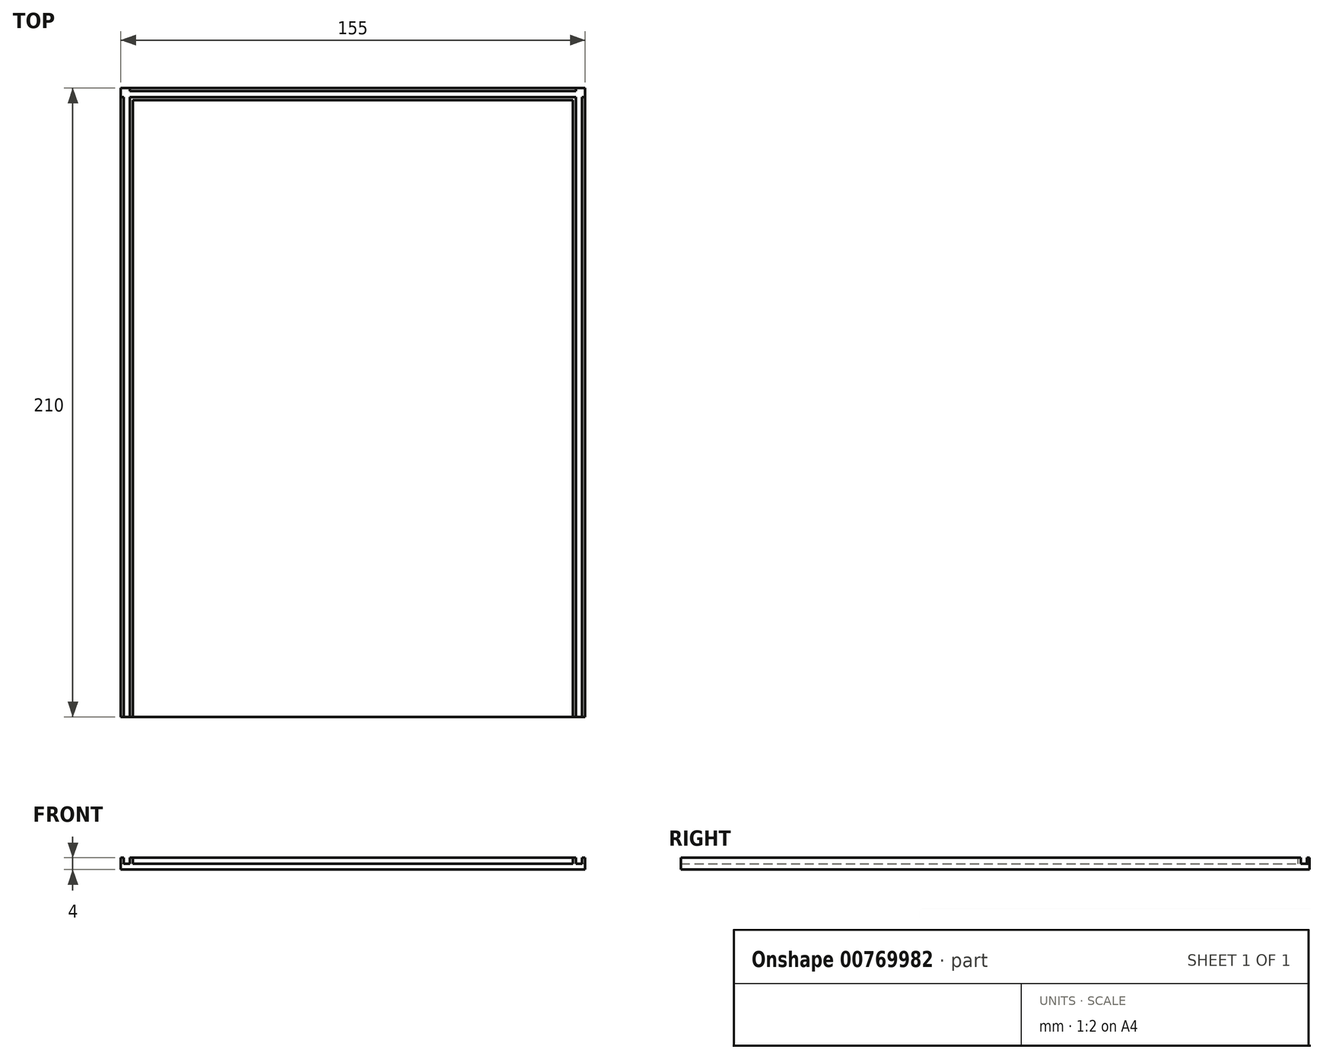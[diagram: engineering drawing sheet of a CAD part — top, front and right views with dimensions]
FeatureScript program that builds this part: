
annotation { "Feature Type Name" : "Feature", "Feature Type Description" : "" }
export const myFeature = defineFeature(function(context is Context, id is Id, definition is map)
    precondition{}
    {
        {
            var Q0;
            Q0=qCreatedBy(makeId("Top.planeOp"),FACE);
            var sketch = newSketch(context, id + "F0", { "sketchPlane" : qUnion([Q0])});
            skPoint(sketch, "E0.middle", {"position": v(0, 0) * mm});
            skLineSegment(sketch, "E1.bottom", {"start": v(77.5, 105) * mm, "end": v(-77.5, 105) * mm});
            skLineSegment(sketch, "E1.top", {"start": v(77.5, -105) * mm, "end": v(-77.5, -105) * mm});
            skLineSegment(sketch, "E1.left", {"start": v(77.5, 105) * mm, "end": v(77.5, -105) * mm});
            skLineSegment(sketch, "E1.right", {"start": v(-77.5, 105) * mm, "end": v(-77.5, -105) * mm});
            skLineSegment(sketch, "E2", {"start": v(-76.5, 105) * mm, "end": v(-76.5, 104) * mm});
            skLineSegment(sketch, "E3", {"start": v(-74.5, 105) * mm, "end": v(-74.5, 104) * mm});
            skLineSegment(sketch, "E4", {"start": v(-73.5, 105) * mm, "end": v(-73.5, 104) * mm});
            skLineSegment(sketch, "E5.MirrorCS", {"start": v(76.5, 105) * mm, "end": v(76.5, 104) * mm});
            skLineSegment(sketch, "E6.MirrorCS", {"start": v(73.5, 105) * mm, "end": v(73.5, 104) * mm});
            skLineSegment(sketch, "E7.MirrorCS", {"start": v(74.5, 105) * mm, "end": v(74.5, 104) * mm});
            skLineSegment(sketch, "E8", {"start": v(-77.5, 104) * mm, "end": v(77.5, 104) * mm});
            skLineSegment(sketch, "E9", {"start": v(-77.5, 102) * mm, "end": v(77.5, 102) * mm});
            skLineSegment(sketch, "E10", {"start": v(-77.5, 101) * mm, "end": v(77.5, 101) * mm});
            skLineSegment(sketch, "E11.trimOffspring", {"start": v(-76.5, 102) * mm, "end": v(-76.5, -105) * mm});
            skLineSegment(sketch, "E12.trimOffspring", {"start": v(-74.5, 102) * mm, "end": v(-74.5, -105) * mm});
            skLineSegment(sketch, "E13.trimOffspring", {"start": v(-73.5, 102) * mm, "end": v(-73.5, -105) * mm});
            skLineSegment(sketch, "E14.trimOffspring", {"start": v(73.5, 102) * mm, "end": v(73.5, -105) * mm});
            skLineSegment(sketch, "E15.trimOffspring", {"start": v(74.5, 102) * mm, "end": v(74.5, -105) * mm});
            skLineSegment(sketch, "E16.trimOffspring", {"start": v(76.5, 102) * mm, "end": v(76.5, -105) * mm});
            skSolve(sketch);
        }
        {
            var Q0;
            {var subQ0=sQuery(id+"F0.wireOp",EDGE,"E13.trimOffspring");var subQ1=sQuery(id+"F0.wireOp",EDGE,"E1.top");var subQ2=makeQuery(id+"F0.imprint","INTERSECT",VERTEX,{"derivedFrom":[subQ1,subQ0]});Q0=makeQuery(id+"F0.imprint","IMPRINT",FACE,{"disambiguationData":[TD([[makeQuery(id+"F0.imprint","IMPRINT",EDGE,{"disambiguationData":[TD([[subQ2,1.0]])],"derivedFrom":subQ1}),-1.0]])]});}
            var Q1;
            {var subQ4=sQuery(id+"F0.wireOp",EDGE,"E8");var subQ6=sQuery(id+"F0.wireOp",EDGE,"E1.left");var subQ7=makeQuery(id+"F0.imprint","INTERSECT",VERTEX,{"derivedFrom":[subQ6,subQ4]});Q1=makeQuery(id+"F0.imprint","IMPRINT",FACE,{"disambiguationData":[TD([[makeQuery(id+"F0.imprint","IMPRINT",EDGE,{"disambiguationData":[TD([[subQ7,-1.0]])],"derivedFrom":subQ6}),-1.0]])]});}
            var Q2;
            {var subQ0=sQuery(id+"F0.wireOp",EDGE,"E15.trimOffspring");var subQ1=sQuery(id+"F0.wireOp",EDGE,"E1.top");var subQ2=makeQuery(id+"F0.imprint","INTERSECT",VERTEX,{"derivedFrom":[subQ1,subQ0]});Q2=makeQuery(id+"F0.imprint","IMPRINT",FACE,{"disambiguationData":[TD([[makeQuery(id+"F0.imprint","IMPRINT",EDGE,{"disambiguationData":[TD([[subQ2,1.0]])],"derivedFrom":subQ1}),-1.0]])]});}
            var Q3;
            {var subQ0=sQuery(id+"F0.wireOp",EDGE,"E11.trimOffspring");var subQ1=sQuery(id+"F0.wireOp",EDGE,"E1.top");var subQ2=makeQuery(id+"F0.imprint","INTERSECT",VERTEX,{"derivedFrom":[subQ1,subQ0]});Q3=makeQuery(id+"F0.imprint","IMPRINT",FACE,{"disambiguationData":[TD([[makeQuery(id+"F0.imprint","IMPRINT",EDGE,{"disambiguationData":[TD([[subQ2,1.0]])],"derivedFrom":subQ1}),-1.0]])]});}
            var Q4;
            {var subQ0=sQuery(id+"F0.wireOp",EDGE,"E13.trimOffspring");var subQ1=sQuery(id+"F0.wireOp",EDGE,"E9");var subQ2=makeQuery(id+"F0.imprint","INTERSECT",VERTEX,{"derivedFrom":[subQ1,subQ0]});Q4=makeQuery(id+"F0.imprint","IMPRINT",FACE,{"disambiguationData":[TD([[makeQuery(id+"F0.imprint","IMPRINT",EDGE,{"disambiguationData":[TD([[subQ2,-1.0]])],"derivedFrom":subQ1}),-1.0]])]});}
            var Q5;
            {var subQ0=sQuery(id+"F0.wireOp",EDGE,"E14.trimOffspring");var subQ1=sQuery(id+"F0.wireOp",EDGE,"E1.top");var subQ2=makeQuery(id+"F0.imprint","INTERSECT",VERTEX,{"derivedFrom":[subQ1,subQ0]});Q5=makeQuery(id+"F0.imprint","IMPRINT",FACE,{"disambiguationData":[TD([[makeQuery(id+"F0.imprint","IMPRINT",EDGE,{"disambiguationData":[TD([[subQ2,1.0]])],"derivedFrom":subQ1}),-1.0]])]});}
            var Q6;
            {var subQ0=sQuery(id+"F0.wireOp",EDGE,"E12.trimOffspring");var subQ1=sQuery(id+"F0.wireOp",EDGE,"E1.top");var subQ2=makeQuery(id+"F0.imprint","INTERSECT",VERTEX,{"derivedFrom":[subQ1,subQ0]});Q6=makeQuery(id+"F0.imprint","IMPRINT",FACE,{"disambiguationData":[TD([[makeQuery(id+"F0.imprint","IMPRINT",EDGE,{"disambiguationData":[TD([[subQ2,1.0]])],"derivedFrom":subQ1}),-1.0]])]});}
            var Q7;
            {var subQ0=sQuery(id+"F0.wireOp",EDGE,"E4");Q7=makeQuery(id+"F0.imprint","IMPRINT",FACE,{"disambiguationData":[TD([[makeQuery(id+"F0.imprint","IMPRINT",EDGE,{"derivedFrom":subQ0}),1.0]])]});}
            var Q8;
            {var subQ0=sQuery(id+"F0.wireOp",EDGE,"E1.right");var subQ1=sQuery(id+"F0.wireOp",EDGE,"E1.top");var subQ2=makeQuery(id+"F0.imprint","INTERSECT",VERTEX,{"derivedFrom":[subQ1,subQ0]});Q8=makeQuery(id+"F0.imprint","IMPRINT",FACE,{"disambiguationData":[TD([[makeQuery(id+"F0.imprint","IMPRINT",EDGE,{"disambiguationData":[TD([[subQ2,1.0]])],"derivedFrom":subQ1}),-1.0]])]});}
            var Q9;
            {var subQ0=sQuery(id+"F0.wireOp",EDGE,"E1.left");var subQ1=sQuery(id+"F0.wireOp",EDGE,"E1.top");var subQ2=makeQuery(id+"F0.imprint","INTERSECT",VERTEX,{"derivedFrom":[subQ1,subQ0]});Q9=makeQuery(id+"F0.imprint","IMPRINT",FACE,{"disambiguationData":[TD([[makeQuery(id+"F0.imprint","IMPRINT",EDGE,{"disambiguationData":[TD([[subQ2,-1.0]])],"derivedFrom":subQ1}),-1.0]])]});}
            var Q10;
            {var subQ0=sQuery(id+"F0.wireOp",EDGE,"E12.trimOffspring");var subQ1=sQuery(id+"F0.wireOp",EDGE,"E9");var subQ2=makeQuery(id+"F0.imprint","INTERSECT",VERTEX,{"derivedFrom":[subQ1,subQ0]});Q10=makeQuery(id+"F0.imprint","IMPRINT",FACE,{"disambiguationData":[TD([[makeQuery(id+"F0.imprint","IMPRINT",EDGE,{"disambiguationData":[TD([[subQ2,-1.0]])],"derivedFrom":subQ1}),-1.0]])]});}
            var Q11;
            {var subQ0=sQuery(id+"F0.wireOp",EDGE,"E15.trimOffspring");var subQ1=sQuery(id+"F0.wireOp",EDGE,"E9");var subQ2=makeQuery(id+"F0.imprint","INTERSECT",VERTEX,{"derivedFrom":[subQ1,subQ0]});Q11=makeQuery(id+"F0.imprint","IMPRINT",FACE,{"disambiguationData":[TD([[makeQuery(id+"F0.imprint","IMPRINT",EDGE,{"disambiguationData":[TD([[subQ2,-1.0]])],"derivedFrom":subQ1}),-1.0]])]});}
            var Q12;
            {var subQ0=sQuery(id+"F0.wireOp",EDGE,"E14.trimOffspring");var subQ1=sQuery(id+"F0.wireOp",EDGE,"E9");var subQ2=makeQuery(id+"F0.imprint","INTERSECT",VERTEX,{"derivedFrom":[subQ1,subQ0]});Q12=makeQuery(id+"F0.imprint","IMPRINT",FACE,{"disambiguationData":[TD([[makeQuery(id+"F0.imprint","IMPRINT",EDGE,{"disambiguationData":[TD([[subQ2,-1.0]])],"derivedFrom":subQ1}),-1.0]])]});}
            var Q13;
            {var subQ0=sQuery(id+"F0.wireOp",EDGE,"E9");var subQ1=sQuery(id+"F0.wireOp",EDGE,"E1.left");var subQ2=makeQuery(id+"F0.imprint","INTERSECT",VERTEX,{"derivedFrom":[subQ1,subQ0]});Q13=makeQuery(id+"F0.imprint","IMPRINT",FACE,{"disambiguationData":[TD([[makeQuery(id+"F0.imprint","IMPRINT",EDGE,{"disambiguationData":[TD([[subQ2,-1.0]])],"derivedFrom":subQ1}),-1.0]])]});}
            var Q14;
            {var subQ0=sQuery(id+"F0.wireOp",EDGE,"E9");var subQ1=sQuery(id+"F0.wireOp",EDGE,"E1.right");var subQ2=makeQuery(id+"F0.imprint","INTERSECT",VERTEX,{"derivedFrom":[subQ1,subQ0]});Q14=makeQuery(id+"F0.imprint","IMPRINT",FACE,{"disambiguationData":[TD([[makeQuery(id+"F0.imprint","IMPRINT",EDGE,{"disambiguationData":[TD([[subQ2,-1.0]])],"derivedFrom":subQ1}),1.0]])]});}
            var Q15;
            {var subQ0=sQuery(id+"F0.wireOp",EDGE,"E3");Q15=makeQuery(id+"F0.imprint","IMPRINT",FACE,{"disambiguationData":[TD([[makeQuery(id+"F0.imprint","IMPRINT",EDGE,{"derivedFrom":subQ0}),1.0]])]});}
            var Q16;
            {var subQ0=sQuery(id+"F0.wireOp",EDGE,"E6.MirrorCS");Q16=makeQuery(id+"F0.imprint","IMPRINT",FACE,{"disambiguationData":[TD([[makeQuery(id+"F0.imprint","IMPRINT",EDGE,{"derivedFrom":subQ0}),1.0]])]});}
            var Q17;
            {var subQ0=sQuery(id+"F0.wireOp",EDGE,"E11.trimOffspring");var subQ1=sQuery(id+"F0.wireOp",EDGE,"E9");var subQ2=makeQuery(id+"F0.imprint","INTERSECT",VERTEX,{"derivedFrom":[subQ1,subQ0]});Q17=makeQuery(id+"F0.imprint","IMPRINT",FACE,{"disambiguationData":[TD([[makeQuery(id+"F0.imprint","IMPRINT",EDGE,{"disambiguationData":[TD([[subQ2,-1.0]])],"derivedFrom":subQ1}),-1.0]])]});}
            var Q18;
            {var subQ0=sQuery(id+"F0.wireOp",EDGE,"E2");Q18=makeQuery(id+"F0.imprint","IMPRINT",FACE,{"disambiguationData":[TD([[makeQuery(id+"F0.imprint","IMPRINT",EDGE,{"derivedFrom":subQ0}),1.0]])]});}
            var Q19;
            {var subQ3=sQuery(id+"F0.wireOp",EDGE,"E2");Q19=makeQuery(id+"F0.imprint","IMPRINT",FACE,{"disambiguationData":[TD([[makeQuery(id+"F0.imprint","IMPRINT",EDGE,{"derivedFrom":subQ3}),-1.0]])]});}
            var Q20;
            {var subQ3=sQuery(id+"F0.wireOp",EDGE,"E5.MirrorCS");Q20=makeQuery(id+"F0.imprint","IMPRINT",FACE,{"disambiguationData":[TD([[makeQuery(id+"F0.imprint","IMPRINT",EDGE,{"derivedFrom":subQ3}),1.0]])]});}
            var Q21;
            {var subQ0=sQuery(id+"F0.wireOp",EDGE,"E5.MirrorCS");Q21=makeQuery(id+"F0.imprint","IMPRINT",FACE,{"disambiguationData":[TD([[makeQuery(id+"F0.imprint","IMPRINT",EDGE,{"derivedFrom":subQ0}),-1.0]])]});}
            extrude(context, id + "F1", {"entities" : qUnion([Q0, Q1, Q2, Q3, Q4, Q5, Q6, Q7, Q8, Q9, Q10, Q11, Q12, Q13, Q14, Q15, Q16, Q17, Q18, Q19, Q20, Q21]), "depth" : 2 * mm, "offsetDistance" : 25 * mm});
        }
        {
            var Q0;
            {var subQ0=sQuery(id+"F0.wireOp",EDGE,"E1.left");var subQ1=sQuery(id+"F0.wireOp",EDGE,"E1.top");var subQ2=makeQuery(id+"F0.imprint","INTERSECT",VERTEX,{"derivedFrom":[subQ1,subQ0]});Q0=makeQuery(id+"F0.imprint","IMPRINT",FACE,{"disambiguationData":[TD([[makeQuery(id+"F0.imprint","IMPRINT",EDGE,{"disambiguationData":[TD([[subQ2,-1.0]])],"derivedFrom":subQ1}),-1.0]])]});}
            var Q1;
            {var subQ0=sQuery(id+"F0.wireOp",EDGE,"E9");var subQ1=sQuery(id+"F0.wireOp",EDGE,"E1.left");var subQ2=makeQuery(id+"F0.imprint","INTERSECT",VERTEX,{"derivedFrom":[subQ1,subQ0]});Q1=makeQuery(id+"F0.imprint","IMPRINT",FACE,{"disambiguationData":[TD([[makeQuery(id+"F0.imprint","IMPRINT",EDGE,{"disambiguationData":[TD([[subQ2,-1.0]])],"derivedFrom":subQ1}),-1.0]])]});}
            var Q2;
            {var subQ0=sQuery(id+"F0.wireOp",EDGE,"E1.right");var subQ1=sQuery(id+"F0.wireOp",EDGE,"E1.top");var subQ2=makeQuery(id+"F0.imprint","INTERSECT",VERTEX,{"derivedFrom":[subQ1,subQ0]});Q2=makeQuery(id+"F0.imprint","IMPRINT",FACE,{"disambiguationData":[TD([[makeQuery(id+"F0.imprint","IMPRINT",EDGE,{"disambiguationData":[TD([[subQ2,1.0]])],"derivedFrom":subQ1}),-1.0]])]});}
            var Q3;
            {var subQ0=sQuery(id+"F0.wireOp",EDGE,"E9");var subQ1=sQuery(id+"F0.wireOp",EDGE,"E1.right");var subQ2=makeQuery(id+"F0.imprint","INTERSECT",VERTEX,{"derivedFrom":[subQ1,subQ0]});Q3=makeQuery(id+"F0.imprint","IMPRINT",FACE,{"disambiguationData":[TD([[makeQuery(id+"F0.imprint","IMPRINT",EDGE,{"disambiguationData":[TD([[subQ2,-1.0]])],"derivedFrom":subQ1}),1.0]])]});}
            var Q4;
            {var subQ0=sQuery(id+"F0.wireOp",EDGE,"E3");Q4=makeQuery(id+"F0.imprint","IMPRINT",FACE,{"disambiguationData":[TD([[makeQuery(id+"F0.imprint","IMPRINT",EDGE,{"derivedFrom":subQ0}),1.0]])]});}
            var Q5;
            {var subQ0=sQuery(id+"F0.wireOp",EDGE,"E6.MirrorCS");Q5=makeQuery(id+"F0.imprint","IMPRINT",FACE,{"disambiguationData":[TD([[makeQuery(id+"F0.imprint","IMPRINT",EDGE,{"derivedFrom":subQ0}),1.0]])]});}
            var Q6;
            {var subQ0=sQuery(id+"F0.wireOp",EDGE,"E4");Q6=makeQuery(id+"F0.imprint","IMPRINT",FACE,{"disambiguationData":[TD([[makeQuery(id+"F0.imprint","IMPRINT",EDGE,{"derivedFrom":subQ0}),1.0]])]});}
            var Q7;
            {var subQ0=sQuery(id+"F0.wireOp",EDGE,"E13.trimOffspring");var subQ1=sQuery(id+"F0.wireOp",EDGE,"E9");var subQ2=makeQuery(id+"F0.imprint","INTERSECT",VERTEX,{"derivedFrom":[subQ1,subQ0]});Q7=makeQuery(id+"F0.imprint","IMPRINT",FACE,{"disambiguationData":[TD([[makeQuery(id+"F0.imprint","IMPRINT",EDGE,{"disambiguationData":[TD([[subQ2,-1.0]])],"derivedFrom":subQ1}),-1.0]])]});}
            var Q8;
            {var subQ0=sQuery(id+"F0.wireOp",EDGE,"E12.trimOffspring");var subQ1=sQuery(id+"F0.wireOp",EDGE,"E1.top");var subQ2=makeQuery(id+"F0.imprint","INTERSECT",VERTEX,{"derivedFrom":[subQ1,subQ0]});Q8=makeQuery(id+"F0.imprint","IMPRINT",FACE,{"disambiguationData":[TD([[makeQuery(id+"F0.imprint","IMPRINT",EDGE,{"disambiguationData":[TD([[subQ2,1.0]])],"derivedFrom":subQ1}),-1.0]])]});}
            var Q9;
            {var subQ0=sQuery(id+"F0.wireOp",EDGE,"E14.trimOffspring");var subQ1=sQuery(id+"F0.wireOp",EDGE,"E1.top");var subQ2=makeQuery(id+"F0.imprint","INTERSECT",VERTEX,{"derivedFrom":[subQ1,subQ0]});Q9=makeQuery(id+"F0.imprint","IMPRINT",FACE,{"disambiguationData":[TD([[makeQuery(id+"F0.imprint","IMPRINT",EDGE,{"disambiguationData":[TD([[subQ2,1.0]])],"derivedFrom":subQ1}),-1.0]])]});}
            var Q10;
            {var subQ0=sQuery(id+"F0.wireOp",EDGE,"E12.trimOffspring");var subQ1=sQuery(id+"F0.wireOp",EDGE,"E9");var subQ2=makeQuery(id+"F0.imprint","INTERSECT",VERTEX,{"derivedFrom":[subQ1,subQ0]});Q10=makeQuery(id+"F0.imprint","IMPRINT",FACE,{"disambiguationData":[TD([[makeQuery(id+"F0.imprint","IMPRINT",EDGE,{"disambiguationData":[TD([[subQ2,-1.0]])],"derivedFrom":subQ1}),-1.0]])]});}
            var Q11;
            {var subQ0=sQuery(id+"F0.wireOp",EDGE,"E14.trimOffspring");var subQ1=sQuery(id+"F0.wireOp",EDGE,"E9");var subQ2=makeQuery(id+"F0.imprint","INTERSECT",VERTEX,{"derivedFrom":[subQ1,subQ0]});Q11=makeQuery(id+"F0.imprint","IMPRINT",FACE,{"disambiguationData":[TD([[makeQuery(id+"F0.imprint","IMPRINT",EDGE,{"disambiguationData":[TD([[subQ2,-1.0]])],"derivedFrom":subQ1}),-1.0]])]});}
            extrude(context, id + "F2", {"entities" : qUnion([Q0, Q1, Q2, Q3, Q4, Q5, Q6, Q7, Q8, Q9, Q10, Q11]), "operationType" : NewBodyOperationType.ADD, "depth" : 4 * mm, "offsetDistance" : 25 * mm});
        }
    });
